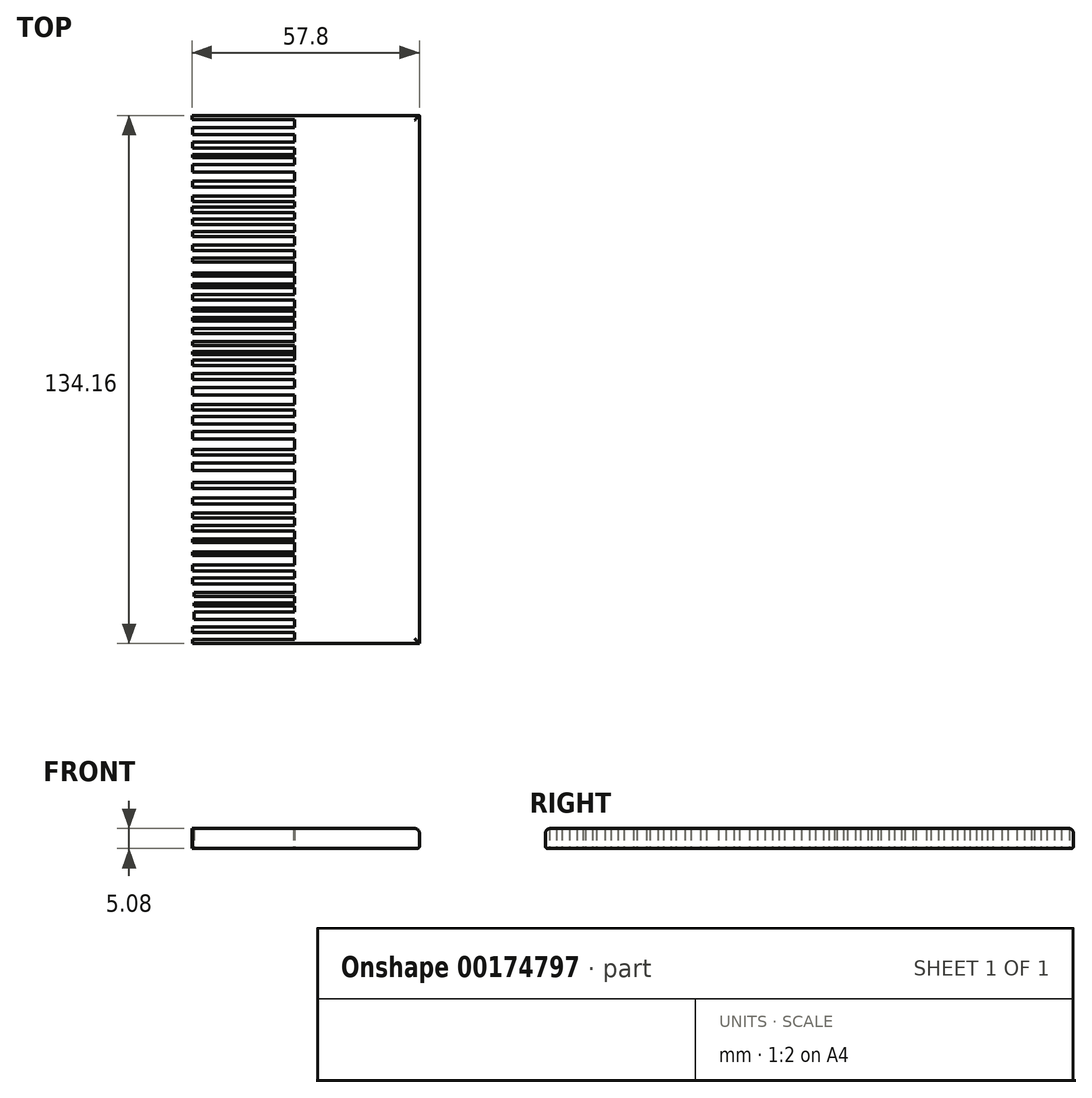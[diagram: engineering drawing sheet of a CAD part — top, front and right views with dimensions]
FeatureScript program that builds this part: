
annotation { "Feature Type Name" : "Feature", "Feature Type Description" : "" }
export const myFeature = defineFeature(function(context is Context, id is Id, definition is map)
    precondition{}
    {
        {
            var Q0;
            Q0=qCreatedBy(makeId("Top.planeOp"),FACE);
            var sketch = newSketch(context, id + "F0", { "sketchPlane" : qUnion([Q0])});
            skLineSegment(sketch, "E0.bottom", {"start": v(13.02, 62.13) * mm, "end": v(44.78, 62.13) * mm});
            skLineSegment(sketch, "E0.top", {"start": v(13.02, -72.03) * mm, "end": v(44.78, -72.03) * mm});
            skLineSegment(sketch, "E0.left", {"start": v(13.02, 62.13) * mm, "end": v(13.02, -72.03) * mm});
            skLineSegment(sketch, "E0.right", {"start": v(44.78, 62.13) * mm, "end": v(44.78, -72.03) * mm});
            skLineSegment(sketch, "E1.bottom", {"start": v(13.02, 62.13) * mm, "end": v(-13.02, 62.13) * mm});
            skLineSegment(sketch, "E1.top", {"start": v(13.02, 61.1) * mm, "end": v(-13.02, 61.1) * mm});
            skLineSegment(sketch, "E1.left", {"start": v(13.02, 62.13) * mm, "end": v(13.02, 61.1) * mm});
            skLineSegment(sketch, "E1.right", {"start": v(-13.02, 62.13) * mm, "end": v(-13.02, 61.1) * mm});
            skLineSegment(sketch, "E2.bottom", {"start": v(13.02, 35.75) * mm, "end": v(-12.84, 35.75) * mm});
            skLineSegment(sketch, "E2.top", {"start": v(13.02, 34.36) * mm, "end": v(-12.84, 34.36) * mm});
            skLineSegment(sketch, "E2.left", {"start": v(13.02, 35.75) * mm, "end": v(13.02, 34.36) * mm});
            skLineSegment(sketch, "E2.right", {"start": v(-12.84, 35.75) * mm, "end": v(-12.84, 34.36) * mm});
            skLineSegment(sketch, "E3.bottom", {"start": v(13.02, 31.41) * mm, "end": v(-12.84, 31.41) * mm});
            skLineSegment(sketch, "E3.top", {"start": v(13.02, 32.63) * mm, "end": v(-12.84, 32.63) * mm});
            skLineSegment(sketch, "E3.left", {"start": v(13.02, 31.41) * mm, "end": v(13.02, 32.63) * mm});
            skLineSegment(sketch, "E3.right", {"start": v(-12.84, 31.41) * mm, "end": v(-12.84, 32.63) * mm});
            skLineSegment(sketch, "E4.bottom", {"start": v(13.02, 29.16) * mm, "end": v(-12.84, 29.16) * mm});
            skLineSegment(sketch, "E4.top", {"start": v(13.02, 27.77) * mm, "end": v(-12.84, 27.77) * mm});
            skLineSegment(sketch, "E4.left", {"start": v(13.02, 29.16) * mm, "end": v(13.02, 27.77) * mm});
            skLineSegment(sketch, "E4.right", {"start": v(-12.84, 29.16) * mm, "end": v(-12.84, 27.77) * mm});
            skLineSegment(sketch, "E5.bottom", {"start": v(13.02, 24.82) * mm, "end": v(-12.84, 24.82) * mm});
            skLineSegment(sketch, "E5.top", {"start": v(13.02, 25.86) * mm, "end": v(-12.84, 25.86) * mm});
            skLineSegment(sketch, "E5.left", {"start": v(13.02, 24.82) * mm, "end": v(13.02, 25.86) * mm});
            skLineSegment(sketch, "E5.right", {"start": v(-12.84, 24.82) * mm, "end": v(-12.84, 25.86) * mm});
            skLineSegment(sketch, "E6.bottom", {"start": v(13.02, 21.35) * mm, "end": v(-12.84, 21.35) * mm});
            skLineSegment(sketch, "E6.top", {"start": v(13.02, 22.04) * mm, "end": v(-12.84, 22.04) * mm});
            skLineSegment(sketch, "E6.left", {"start": v(13.02, 21.35) * mm, "end": v(13.02, 22.04) * mm});
            skLineSegment(sketch, "E6.right", {"start": v(-12.84, 21.35) * mm, "end": v(-12.84, 22.04) * mm});
            skLineSegment(sketch, "E7.bottom", {"start": v(13.02, 19.26) * mm, "end": v(-12.84, 19.26) * mm});
            skLineSegment(sketch, "E7.top", {"start": v(13.02, 18.4) * mm, "end": v(-12.84, 18.4) * mm});
            skLineSegment(sketch, "E7.left", {"start": v(13.02, 19.26) * mm, "end": v(13.02, 18.4) * mm});
            skLineSegment(sketch, "E7.right", {"start": v(-12.84, 19.26) * mm, "end": v(-12.84, 18.4) * mm});
            skLineSegment(sketch, "E8.bottom", {"start": v(14.75, 16.66) * mm, "end": v(-12.84, 16.66) * mm});
            skLineSegment(sketch, "E8.top", {"start": v(14.75, 15.27) * mm, "end": v(-12.84, 15.27) * mm});
            skLineSegment(sketch, "E8.left", {"start": v(14.75, 16.66) * mm, "end": v(14.75, 15.27) * mm});
            skLineSegment(sketch, "E8.right", {"start": v(-12.84, 16.66) * mm, "end": v(-12.84, 15.27) * mm});
            skLineSegment(sketch, "E9.bottom", {"start": v(13.02, 12.5) * mm, "end": v(-12.84, 12.5) * mm});
            skLineSegment(sketch, "E9.top", {"start": v(13.02, 13.2) * mm, "end": v(-12.84, 13.2) * mm});
            skLineSegment(sketch, "E9.left", {"start": v(13.02, 12.5) * mm, "end": v(13.02, 13.2) * mm});
            skLineSegment(sketch, "E9.right", {"start": v(-12.84, 12.5) * mm, "end": v(-12.84, 13.2) * mm});
            skLineSegment(sketch, "E10.bottom", {"start": v(13.02, 9.9) * mm, "end": v(-12.84, 9.9) * mm});
            skLineSegment(sketch, "E10.top", {"start": v(13.02, 10.76) * mm, "end": v(-12.84, 10.76) * mm});
            skLineSegment(sketch, "E10.left", {"start": v(13.02, 9.9) * mm, "end": v(13.02, 10.76) * mm});
            skLineSegment(sketch, "E10.right", {"start": v(-12.84, 9.9) * mm, "end": v(-12.84, 10.76) * mm});
            skLineSegment(sketch, "E11.bottom", {"start": v(13.02, 7.98) * mm, "end": v(-12.84, 7.98) * mm});
            skLineSegment(sketch, "E11.top", {"start": v(13.02, 6.77) * mm, "end": v(-12.84, 6.77) * mm});
            skLineSegment(sketch, "E11.left", {"start": v(13.02, 7.98) * mm, "end": v(13.02, 6.77) * mm});
            skLineSegment(sketch, "E11.right", {"start": v(-12.84, 7.98) * mm, "end": v(-12.84, 6.77) * mm});
            skLineSegment(sketch, "E12.bottom", {"start": v(13.02, 4.69) * mm, "end": v(-12.84, 4.69) * mm});
            skLineSegment(sketch, "E12.top", {"start": v(13.02, 3.64) * mm, "end": v(-12.84, 3.64) * mm});
            skLineSegment(sketch, "E12.left", {"start": v(13.02, 4.69) * mm, "end": v(13.02, 3.64) * mm});
            skLineSegment(sketch, "E12.right", {"start": v(-12.84, 4.69) * mm, "end": v(-12.84, 3.64) * mm});
            skLineSegment(sketch, "E13.bottom", {"start": v(13.02, 0) * mm, "end": v(-12.84, 0) * mm});
            skLineSegment(sketch, "E13.top", {"start": v(13.02, -1.39) * mm, "end": v(-12.84, -1.39) * mm});
            skLineSegment(sketch, "E13.left", {"start": v(13.02, 0) * mm, "end": v(13.02, -1.39) * mm});
            skLineSegment(sketch, "E13.right", {"start": v(-12.84, 0) * mm, "end": v(-12.84, -1.39) * mm});
            skLineSegment(sketch, "E14.bottom", {"start": v(13.02, -4.95) * mm, "end": v(-12.84, -4.95) * mm});
            skLineSegment(sketch, "E14.top", {"start": v(13.02, -3.47) * mm, "end": v(-12.84, -3.47) * mm});
            skLineSegment(sketch, "E14.left", {"start": v(13.02, -4.95) * mm, "end": v(13.02, -3.47) * mm});
            skLineSegment(sketch, "E14.right", {"start": v(-12.84, -4.95) * mm, "end": v(-12.84, -3.47) * mm});
            skLineSegment(sketch, "E15.bottom", {"start": v(13.02, -6.94) * mm, "end": v(-12.84, -6.94) * mm});
            skLineSegment(sketch, "E15.top", {"start": v(13.02, -8.85) * mm, "end": v(-12.84, -8.85) * mm});
            skLineSegment(sketch, "E15.left", {"start": v(13.02, -6.94) * mm, "end": v(13.02, -8.85) * mm});
            skLineSegment(sketch, "E15.right", {"start": v(-12.84, -6.94) * mm, "end": v(-12.84, -8.85) * mm});
            skLineSegment(sketch, "E16.bottom", {"start": v(13.02, -11.28) * mm, "end": v(-12.84, -11.28) * mm});
            skLineSegment(sketch, "E16.top", {"start": v(13.02, -12.67) * mm, "end": v(-12.84, -12.67) * mm});
            skLineSegment(sketch, "E16.left", {"start": v(13.02, -11.28) * mm, "end": v(13.02, -12.67) * mm});
            skLineSegment(sketch, "E16.right", {"start": v(-12.84, -11.28) * mm, "end": v(-12.84, -12.67) * mm});
            skLineSegment(sketch, "E17.bottom", {"start": v(13.02, -16.31) * mm, "end": v(-12.84, -16.31) * mm});
            skLineSegment(sketch, "E17.top", {"start": v(13.02, -14.4) * mm, "end": v(-12.84, -14.4) * mm});
            skLineSegment(sketch, "E17.left", {"start": v(13.02, -16.31) * mm, "end": v(13.02, -14.4) * mm});
            skLineSegment(sketch, "E17.right", {"start": v(-12.84, -16.31) * mm, "end": v(-12.84, -14.4) * mm});
            skLineSegment(sketch, "E18.bottom", {"start": v(13.02, -18.22) * mm, "end": v(-12.84, -18.22) * mm});
            skLineSegment(sketch, "E18.top", {"start": v(13.02, -20.13) * mm, "end": v(-12.84, -20.13) * mm});
            skLineSegment(sketch, "E18.left", {"start": v(13.02, -18.22) * mm, "end": v(13.02, -20.13) * mm});
            skLineSegment(sketch, "E18.right", {"start": v(-12.84, -18.22) * mm, "end": v(-12.84, -20.13) * mm});
            skLineSegment(sketch, "E19.bottom", {"start": v(13.02, -22.74) * mm, "end": v(-12.84, -22.74) * mm});
            skLineSegment(sketch, "E19.top", {"start": v(13.02, -24.12) * mm, "end": v(-12.84, -24.12) * mm});
            skLineSegment(sketch, "E19.left", {"start": v(13.02, -22.74) * mm, "end": v(13.02, -24.12) * mm});
            skLineSegment(sketch, "E19.right", {"start": v(-12.84, -22.74) * mm, "end": v(-12.84, -24.12) * mm});
            skLineSegment(sketch, "E20.bottom", {"start": v(13.02, -26.2) * mm, "end": v(-12.84, -26.2) * mm});
            skLineSegment(sketch, "E20.top", {"start": v(13.02, -28.12) * mm, "end": v(-12.84, -28.12) * mm});
            skLineSegment(sketch, "E20.left", {"start": v(13.02, -26.2) * mm, "end": v(13.02, -28.12) * mm});
            skLineSegment(sketch, "E20.right", {"start": v(-12.84, -26.2) * mm, "end": v(-12.84, -28.12) * mm});
            skLineSegment(sketch, "E21.bottom", {"start": v(13.02, -31.07) * mm, "end": v(-12.84, -31.07) * mm});
            skLineSegment(sketch, "E21.top", {"start": v(13.02, -32.63) * mm, "end": v(-12.84, -32.63) * mm});
            skLineSegment(sketch, "E21.left", {"start": v(13.02, -31.07) * mm, "end": v(13.02, -32.63) * mm});
            skLineSegment(sketch, "E21.right", {"start": v(-12.84, -31.07) * mm, "end": v(-12.84, -32.63) * mm});
            skLineSegment(sketch, "E22.bottom", {"start": v(13.02, -35.06) * mm, "end": v(-12.84, -35.06) * mm});
            skLineSegment(sketch, "E22.top", {"start": v(13.02, -36.62) * mm, "end": v(-12.84, -36.62) * mm});
            skLineSegment(sketch, "E22.left", {"start": v(13.02, -35.06) * mm, "end": v(13.02, -36.62) * mm});
            skLineSegment(sketch, "E22.right", {"start": v(-12.84, -35.06) * mm, "end": v(-12.84, -36.62) * mm});
            skLineSegment(sketch, "E23.bottom", {"start": v(13.02, -38.88) * mm, "end": v(-12.84, -38.88) * mm});
            skLineSegment(sketch, "E23.top", {"start": v(13.02, -40.1) * mm, "end": v(-12.84, -40.1) * mm});
            skLineSegment(sketch, "E23.left", {"start": v(13.02, -38.88) * mm, "end": v(13.02, -40.1) * mm});
            skLineSegment(sketch, "E23.right", {"start": v(-12.84, -38.88) * mm, "end": v(-12.84, -40.1) * mm});
            skLineSegment(sketch, "E24.bottom", {"start": v(13.02, -42) * mm, "end": v(-12.84, -42) * mm});
            skLineSegment(sketch, "E24.top", {"start": v(13.02, -43.39) * mm, "end": v(-12.84, -43.39) * mm});
            skLineSegment(sketch, "E24.left", {"start": v(13.02, -42) * mm, "end": v(13.02, -43.39) * mm});
            skLineSegment(sketch, "E24.right", {"start": v(-12.84, -42) * mm, "end": v(-12.84, -43.39) * mm});
            skLineSegment(sketch, "E25.bottom", {"start": v(13.02, -45.47) * mm, "end": v(-12.84, -45.47) * mm});
            skLineSegment(sketch, "E25.top", {"start": v(13.02, -46.34) * mm, "end": v(-12.84, -46.34) * mm});
            skLineSegment(sketch, "E25.left", {"start": v(13.02, -45.47) * mm, "end": v(13.02, -46.34) * mm});
            skLineSegment(sketch, "E25.right", {"start": v(-12.84, -45.47) * mm, "end": v(-12.84, -46.34) * mm});
            skLineSegment(sketch, "E26.bottom", {"start": v(13.02, -48.77) * mm, "end": v(-12.84, -48.77) * mm});
            skLineSegment(sketch, "E26.top", {"start": v(13.02, -49.64) * mm, "end": v(-12.84, -49.64) * mm});
            skLineSegment(sketch, "E26.left", {"start": v(13.02, -48.77) * mm, "end": v(13.02, -49.64) * mm});
            skLineSegment(sketch, "E26.right", {"start": v(-12.84, -48.77) * mm, "end": v(-12.84, -49.64) * mm});
            skLineSegment(sketch, "E27.bottom", {"start": v(13.02, -72.03) * mm, "end": v(-12.84, -72.03) * mm});
            skLineSegment(sketch, "E27.top", {"start": v(13.02, -70.99) * mm, "end": v(-12.84, -70.99) * mm});
            skLineSegment(sketch, "E27.left", {"start": v(13.02, -72.03) * mm, "end": v(13.02, -70.99) * mm});
            skLineSegment(sketch, "E27.right", {"start": v(-12.84, -72.03) * mm, "end": v(-12.84, -70.99) * mm});
            skLineSegment(sketch, "E28", {"start": v(13.02, 35.75) * mm, "end": v(13.02, 37.49) * mm});
            skLineSegment(sketch, "E29.bottom", {"start": v(13.02, 37.49) * mm, "end": v(-13.02, 37.49) * mm});
            skLineSegment(sketch, "E29.top", {"start": v(13.02, 38.88) * mm, "end": v(-13.02, 38.88) * mm});
            skLineSegment(sketch, "E29.left", {"start": v(13.02, 37.49) * mm, "end": v(13.02, 38.88) * mm});
            skLineSegment(sketch, "E29.right", {"start": v(-13.02, 37.49) * mm, "end": v(-13.02, 38.88) * mm});
            skLineSegment(sketch, "E30.bottom", {"start": v(13.02, -69.25) * mm, "end": v(-12.84, -69.25) * mm});
            skLineSegment(sketch, "E30.top", {"start": v(13.02, -67.86) * mm, "end": v(-12.84, -67.86) * mm});
            skLineSegment(sketch, "E30.left", {"start": v(13.02, -69.25) * mm, "end": v(13.02, -67.86) * mm});
            skLineSegment(sketch, "E30.right", {"start": v(-12.84, -69.25) * mm, "end": v(-12.84, -67.86) * mm});
            skLineSegment(sketch, "E31.bottom", {"start": v(13.02, -65.95) * mm, "end": v(-12.5, -65.95) * mm});
            skLineSegment(sketch, "E31.top", {"start": v(13.02, -64.04) * mm, "end": v(-12.5, -64.04) * mm});
            skLineSegment(sketch, "E31.left", {"start": v(13.02, -65.95) * mm, "end": v(13.02, -64.04) * mm});
            skLineSegment(sketch, "E31.right", {"start": v(-12.5, -65.95) * mm, "end": v(-12.5, -64.04) * mm});
            skLineSegment(sketch, "E32.bottom", {"start": v(13.02, -62.48) * mm, "end": v(-12.5, -62.48) * mm});
            skLineSegment(sketch, "E32.top", {"start": v(13.02, -61.79) * mm, "end": v(-12.5, -61.79) * mm});
            skLineSegment(sketch, "E32.left", {"start": v(13.02, -62.48) * mm, "end": v(13.02, -61.79) * mm});
            skLineSegment(sketch, "E32.right", {"start": v(-12.5, -62.48) * mm, "end": v(-12.5, -61.79) * mm});
            skLineSegment(sketch, "E33.bottom", {"start": v(13.02, -60.05) * mm, "end": v(-12.5, -60.05) * mm});
            skLineSegment(sketch, "E33.top", {"start": v(13.02, -59) * mm, "end": v(-12.5, -59) * mm});
            skLineSegment(sketch, "E33.left", {"start": v(13.02, -60.05) * mm, "end": v(13.02, -59) * mm});
            skLineSegment(sketch, "E33.right", {"start": v(-12.5, -60.05) * mm, "end": v(-12.5, -59) * mm});
            skLineSegment(sketch, "E34.bottom", {"start": v(13.02, -56.93) * mm, "end": v(-12.84, -56.93) * mm});
            skLineSegment(sketch, "E34.top", {"start": v(13.02, -55.36) * mm, "end": v(-12.84, -55.36) * mm});
            skLineSegment(sketch, "E34.left", {"start": v(13.02, -56.93) * mm, "end": v(13.02, -55.36) * mm});
            skLineSegment(sketch, "E34.right", {"start": v(-12.84, -56.93) * mm, "end": v(-12.84, -55.36) * mm});
            skLineSegment(sketch, "E35.bottom", {"start": v(13.02, -53.63) * mm, "end": v(-12.84, -53.63) * mm});
            skLineSegment(sketch, "E35.top", {"start": v(13.02, -52.07) * mm, "end": v(-12.84, -52.07) * mm});
            skLineSegment(sketch, "E35.left", {"start": v(13.02, -53.63) * mm, "end": v(13.02, -52.07) * mm});
            skLineSegment(sketch, "E35.right", {"start": v(-12.84, -53.63) * mm, "end": v(-12.84, -52.07) * mm});
            skLineSegment(sketch, "E36.bottom", {"start": v(13.02, 41.65) * mm, "end": v(-12.84, 41.65) * mm});
            skLineSegment(sketch, "E36.top", {"start": v(13.02, 40.27) * mm, "end": v(-12.84, 40.27) * mm});
            skLineSegment(sketch, "E36.left", {"start": v(13.02, 41.65) * mm, "end": v(13.02, 40.27) * mm});
            skLineSegment(sketch, "E36.right", {"start": v(-12.84, 41.65) * mm, "end": v(-12.84, 40.27) * mm});
            skLineSegment(sketch, "E37.bottom", {"start": v(13.02, 43.91) * mm, "end": v(-12.84, 43.91) * mm});
            skLineSegment(sketch, "E37.top", {"start": v(13.02, 45.47) * mm, "end": v(-12.84, 45.47) * mm});
            skLineSegment(sketch, "E37.left", {"start": v(13.02, 43.91) * mm, "end": v(13.02, 45.47) * mm});
            skLineSegment(sketch, "E37.right", {"start": v(-12.84, 43.91) * mm, "end": v(-12.84, 45.47) * mm});
            skLineSegment(sketch, "E38.bottom", {"start": v(13.02, 47.73) * mm, "end": v(-12.84, 47.73) * mm});
            skLineSegment(sketch, "E38.top", {"start": v(13.02, 49.64) * mm, "end": v(-12.84, 49.64) * mm});
            skLineSegment(sketch, "E38.left", {"start": v(13.02, 47.73) * mm, "end": v(13.02, 49.64) * mm});
            skLineSegment(sketch, "E38.right", {"start": v(-12.84, 47.73) * mm, "end": v(-12.84, 49.64) * mm});
            skLineSegment(sketch, "E39.bottom", {"start": v(13.02, 51.37) * mm, "end": v(-12.84, 51.37) * mm});
            skLineSegment(sketch, "E39.top", {"start": v(13.02, 52.24) * mm, "end": v(-12.84, 52.24) * mm});
            skLineSegment(sketch, "E39.left", {"start": v(13.02, 51.37) * mm, "end": v(13.02, 52.24) * mm});
            skLineSegment(sketch, "E39.right", {"start": v(-12.84, 51.37) * mm, "end": v(-12.84, 52.24) * mm});
            skLineSegment(sketch, "E40.bottom", {"start": v(13.02, 53.8) * mm, "end": v(-12.84, 53.8) * mm});
            skLineSegment(sketch, "E40.top", {"start": v(13.02, 55.36) * mm, "end": v(-12.84, 55.36) * mm});
            skLineSegment(sketch, "E40.left", {"start": v(13.02, 53.8) * mm, "end": v(13.02, 55.36) * mm});
            skLineSegment(sketch, "E40.right", {"start": v(-12.84, 53.8) * mm, "end": v(-12.84, 55.36) * mm});
            skLineSegment(sketch, "E41.bottom", {"start": v(13.02, 57.27) * mm, "end": v(-12.84, 57.27) * mm});
            skLineSegment(sketch, "E41.top", {"start": v(13.02, 59) * mm, "end": v(-12.84, 59) * mm});
            skLineSegment(sketch, "E41.left", {"start": v(13.02, 57.27) * mm, "end": v(13.02, 59) * mm});
            skLineSegment(sketch, "E41.right", {"start": v(-12.84, 57.27) * mm, "end": v(-12.84, 59) * mm});
            skLineSegment(sketch, "E42.bottom", {"start": v(12.84, 1.39) * mm, "end": v(-12.84, 1.39) * mm});
            skLineSegment(sketch, "E42.top", {"start": v(12.84, 2.08) * mm, "end": v(-12.84, 2.08) * mm});
            skLineSegment(sketch, "E42.left", {"start": v(12.84, 1.39) * mm, "end": v(12.84, 2.08) * mm});
            skLineSegment(sketch, "E42.right", {"start": v(-12.84, 1.39) * mm, "end": v(-12.84, 2.08) * mm});
            skSolve(sketch);
        }
        {
            var Q0;
            Q0=makeQuery(id+"F0.imprint","IMPRINT",FACE,{"disambiguationData":[TD([[makeQuery(id+"F0.imprint","IMPRINT",EDGE,{"derivedFrom":sQuery(id+"F0.wireOp",EDGE,"E0.bottom")}),-1.0]])]});
            extrude(context, id + "F1", {"entities" : qUnion([Q0]), "depth" : 5.08 * mm});
        }
        {
            var Q0;
            Q0 = qSketchRegion(id + "F0", true);
            extrude(context, id + "F2", {"entities" : qUnion([Q0]), "operationType" : NewBodyOperationType.ADD, "depth" : 5.08 * mm});
        }
        {
            var Q0;
            {var subQ0=sQuery(id+"F0.wireOp",EDGE,"E0.bottom");Q0=makeQuery(id+"F2.boolean.opBoolean","MERGE",EDGE,{"derivedFrom":[makeQuery(id+"F1.opExtrude","CAP_EDGE",EDGE,{"disambiguationData":[OSD([subQ0])],"isStart":false}),makeQuery(id+"F2.opExtrude","CAP_EDGE",EDGE,{"disambiguationData":[OSD([subQ0,sQuery(id+"F0.wireOp",EDGE,"E1.bottom")])],"isStart":false})]});}
            var Q1;
            Q1=makeQuery(id+"F1.opExtrude","CAP_EDGE",EDGE,{"disambiguationData":[OSD([sQuery(id+"F0.wireOp",EDGE,"E0.right")])],"isStart":false});
            var Q2;
            {var subQ0=sQuery(id+"F0.wireOp",EDGE,"E0.top");Q2=makeQuery(id+"F2.boolean.opBoolean","MERGE",EDGE,{"derivedFrom":[makeQuery(id+"F1.opExtrude","CAP_EDGE",EDGE,{"disambiguationData":[OSD([subQ0])],"isStart":false}),makeQuery(id+"F2.opExtrude","CAP_EDGE",EDGE,{"disambiguationData":[OSD([subQ0,sQuery(id+"F0.wireOp",EDGE,"E27.bottom")])],"isStart":false})]});}
            fillet(context, id + "F3", {"entities" : qUnion([Q0, Q1, Q2]), "radius" : 1.23 * mm, "tangentPropagation" : true, "allowEdgeOverflow" : false});
        }
        {
            var Q0;
            {var subQ0=sQuery(id+"F0.wireOp",EDGE,"E0.top");Q0=makeQuery(id+"F2.boolean.opBoolean","MERGE",EDGE,{"derivedFrom":[makeQuery(id+"F1.opExtrude","CAP_EDGE",EDGE,{"disambiguationData":[OSD([subQ0])],"isStart":true}),makeQuery(id+"F2.opExtrude","CAP_EDGE",EDGE,{"disambiguationData":[OSD([subQ0,sQuery(id+"F0.wireOp",EDGE,"E27.bottom")])],"isStart":true})]});}
            var Q1;
            Q1=makeQuery(id+"F1.opExtrude","CAP_EDGE",EDGE,{"disambiguationData":[OSD([sQuery(id+"F0.wireOp",EDGE,"E0.right")])],"isStart":true});
            var Q2;
            {var subQ0=sQuery(id+"F0.wireOp",EDGE,"E0.bottom");Q2=makeQuery(id+"F2.boolean.opBoolean","MERGE",EDGE,{"derivedFrom":[makeQuery(id+"F1.opExtrude","CAP_EDGE",EDGE,{"disambiguationData":[OSD([subQ0])],"isStart":true}),makeQuery(id+"F2.opExtrude","CAP_EDGE",EDGE,{"disambiguationData":[OSD([subQ0,sQuery(id+"F0.wireOp",EDGE,"E1.bottom")])],"isStart":true})]});}
            fillet(context, id + "F4", {"entities" : qUnion([Q0, Q1, Q2]), "radius" : 0.61 * mm, "tangentPropagation" : true, "allowEdgeOverflow" : false});
        }
    });
